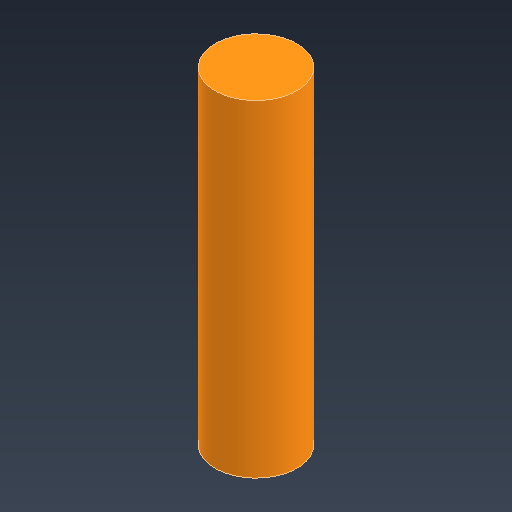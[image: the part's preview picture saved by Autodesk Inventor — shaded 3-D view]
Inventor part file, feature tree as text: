
AUTODESK INVENTOR PART (.ipt)
format: ipt  version: 2021.3 (Build 253353000, 353)  size: 78,336 bytes
history: native  units: in
note: dims shown in document units (in); Inventor stores cm internally (conversion verified against a paired STEP export)
features: extrude x1, sketch x1
ambient origin geometry x8: Origin, YZ Plane, XZ Plane, XY Plane, X Axis, Y Axis, Z Axis, Center Point
bodies: Solid1 (feature_tree)
feature tree (2):
  extrude  "Extrusion1"  Depth=4.0in TaperAngle=0.0deg
  sketch  "Sketch1"  dims[d0=1.0in d1=4.0in d2=0.0in]
